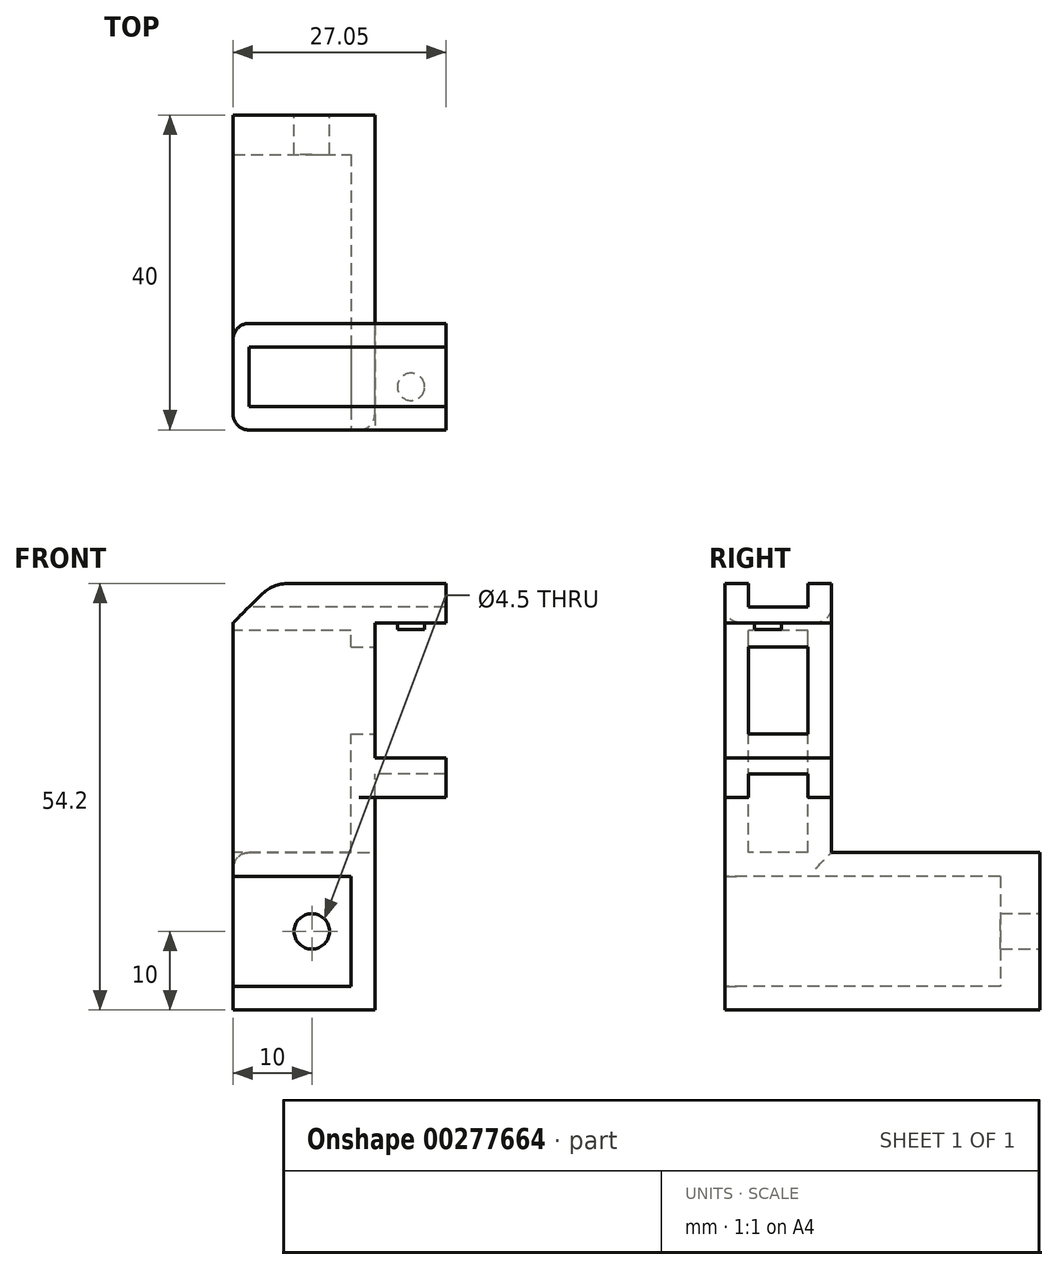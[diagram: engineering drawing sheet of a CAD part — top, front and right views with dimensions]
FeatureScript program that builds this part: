
annotation { "Feature Type Name" : "Feature", "Feature Type Description" : "" }
export const myFeature = defineFeature(function(context is Context, id is Id, definition is map)
    precondition{}
    {
        {
            var Q0;
            Q0=qCreatedBy(makeId("Front.planeOp"),FACE);
            var sketch = newSketch(context, id + "F0", { "sketchPlane" : qUnion([Q0])});
            skLineSegment(sketch, "E0.bottom", {"start": v(0, 0) * mm, "end": v(18, 0) * mm});
            skLineSegment(sketch, "E0.top", {"start": v(0, -21.2) * mm, "end": v(18, -21.2) * mm});
            skLineSegment(sketch, "E0.left", {"start": v(0, 0) * mm, "end": v(0, -21.2) * mm});
            skLineSegment(sketch, "E0.right", {"start": v(18, 0) * mm, "end": v(18, -21.2) * mm});
            skSolve(sketch);
        }
        {
            var Q0;
            Q0 = qSketchRegion(id + "F0", true);
            extrude(context, id + "F1", {"entities" : qUnion([Q0]), "depth" : 40 * mm});
        }
        {
            var Q0;
            Q0=makeQuery(id+"F1.opExtrude","SWEPT_FACE",FACE,{"disambiguationData":[OSD([sQuery(id+"F0.wireOp",EDGE,"E0.right")])]});
            var sketch = newSketch(context, id + "F2", { "sketchPlane" : qUnion([Q0])});
            skLineSegment(sketch, "E1", {"start": v(-40, 0) * mm, "end": v(-26.47, 0) * mm});
            skLineSegment(sketch, "E2", {"start": v(-40, -21.2) * mm, "end": v(-26.47, -21.2) * mm});
            skLineSegment(sketch, "E3", {"start": v(-40, -21.2) * mm, "end": v(-40, -19.15) * mm});
            skLineSegment(sketch, "E4", {"start": v(-26.47, 0) * mm, "end": v(-26.47, -2.05) * mm});
            skLineSegment(sketch, "E5", {"start": v(-26.47, -2.05) * mm, "end": v(-40, -2.05) * mm});
            skLineSegment(sketch, "E6", {"start": v(-40, -2.05) * mm, "end": v(-40, 0) * mm});
            skLineSegment(sketch, "E7", {"start": v(-26.47, -21.2) * mm, "end": v(-26.47, -19.15) * mm});
            skLineSegment(sketch, "E8", {"start": v(-26.47, -19.15) * mm, "end": v(-40, -19.15) * mm});
            skSolve(sketch);
        }
        {
            var Q0;
            Q0 = qSketchRegion(id + "F2", true);
            extrude(context, id + "F3", {"entities" : qUnion([Q0]), "operationType" : NewBodyOperationType.ADD, "depth" : (9.15 - 0.1) * mm});
        }
        {
            var Q0;
            Q0=makeQuery(id+"F3.opExtrude","SWEPT_FACE",FACE,{"disambiguationData":[OSD([sQuery(id+"F2.wireOp",EDGE,"E5")])]});
            var sketch = newSketch(context, id + "F4", { "sketchPlane" : qUnion([Q0])});
            skCircle(sketch, "E9", {"center": v(22.6, 34.53) * mm, "radius": 1.73 * mm});
            skSolve(sketch);
        }
        {
            var Q0;
            Q0 = qSketchRegion(id + "F4", true);
            extrude(context, id + "F5", {"entities" : qUnion([Q0]), "operationType" : NewBodyOperationType.ADD, "depth" : (1 - 0.2) * mm});
        }
        {
            var Q0;
            Q0=makeQuery(id+"F3.opExtrude","SWEPT_FACE",FACE,{"disambiguationData":[OSD([sQuery(id+"F2.wireOp",EDGE,"E5")])]});
            var Q1;
            Q1=makeQuery(id+"F3.opExtrude","SWEPT_FACE",FACE,{"disambiguationData":[OSD([sQuery(id+"F2.wireOp",EDGE,"E8")])]});
            cPlane(context, id + "F6", {"entities" : qUnion([Q0, Q1]), "cplaneType" : CPlaneType.MID_PLANE, "offset" : 25 * mm, "width" : 150 * mm, "height" : 150 * mm});
        }
        {
            var Q0;
            Q0=makeQuery(id+"F3.boolean.opBoolean","MERGE",FACE,{"derivedFrom":[makeQuery(id+"F1.opExtrude","SWEPT_FACE",FACE,{"disambiguationData":[OSD([sQuery(id+"F0.wireOp",EDGE,"E0.top")])]}),makeQuery(id+"F3.opExtrude","SWEPT_FACE",FACE,{"disambiguationData":[OSD([sQuery(id+"F2.wireOp",EDGE,"E2")])]})]});
            var sketch = newSketch(context, id + "F7", { "sketchPlane" : qUnion([Q0])});
            skLineSegment(sketch, "E10.bottom", {"start": v(0, 40) * mm, "end": v(18, 40) * mm});
            skLineSegment(sketch, "E10.top", {"start": v(0, 26.47) * mm, "end": v(18, 26.47) * mm});
            skLineSegment(sketch, "E10.left", {"start": v(0, 40) * mm, "end": v(0, 26.47) * mm});
            skLineSegment(sketch, "E10.right", {"start": v(18, 40) * mm, "end": v(18, 26.47) * mm});
            skSolve(sketch);
        }
        {
            var Q0;
            Q0=makeQuery(id+"F7.imprint","IMPRINT",FACE,{"disambiguationData":[TD([[makeQuery(id+"F7.imprint","IMPRINT",EDGE,{"derivedFrom":sQuery(id+"F7.wireOp",EDGE,"E10.bottom")}),-1.0]])]});
            extrude(context, id + "F8", {"entities" : qUnion([Q0]), "operationType" : NewBodyOperationType.ADD, "depth" : 30 * mm});
        }
        {
            var Q0;
            Q0=makeQuery(id+"F8.opExtrude","SWEPT_FACE",FACE,{"disambiguationData":[OSD([sQuery(id+"F7.wireOp",EDGE,"E10.top")])]});
            var sketch = newSketch(context, id + "F9", { "sketchPlane" : qUnion([Q0])});
            skLineSegment(sketch, "E11.bottom", {"start": v(0, -51.2) * mm, "end": v(-18, -51.2) * mm});
            skLineSegment(sketch, "E11.top", {"start": v(0, -31.2) * mm, "end": v(-18, -31.2) * mm});
            skLineSegment(sketch, "E11.left", {"start": v(0, -51.2) * mm, "end": v(0, -31.2) * mm});
            skLineSegment(sketch, "E11.right", {"start": v(-18, -51.2) * mm, "end": v(-18, -31.2) * mm});
            skSolve(sketch);
        }
        {
            var Q0;
            Q0 = qSketchRegion(id + "F9", true);
            var Q1;
            Q1=qCreatedBy(makeId("Origin.pointOp"),VERTEX);
            extrude(context, id + "F10", {"entities" : qUnion([Q0]), "operationType" : NewBodyOperationType.ADD, "endBound" : BoundingType.UP_TO_VERTEX, "endBoundEntityVertex" : qUnion([Q1]), "depth" : 25 * mm});
        }
        {
            var Q0;
            {var subQ1=sQuery(id+"F0.wireOp",EDGE,"E0.left");var subQ2=sQuery(id+"F0.wireOp",EDGE,"E0.top");var subQ3=makeQuery(id+"F1.opExtrude","SWEPT_FACE",FACE,{"disambiguationData":[OSD([subQ2])]});var subQ4=makeQuery(id+"F3.opExtrude","SWEPT_FACE",FACE,{"disambiguationData":[OSD([sQuery(id+"F2.wireOp",EDGE,"E2")])]});Q0=makeQuery(id+"F8.boolean.opBoolean","SPLIT",FACE,{"disambiguationData":[TD([makeQuery(id+"F1.opExtrude","SWEPT_FACE",FACE,{"disambiguationData":[OSD([subQ1])]})])],"derivedFrom":makeQuery(id+"F3.boolean.opBoolean","MERGE",FACE,{"derivedFrom":[subQ3,subQ4]})});}
            var sketch = newSketch(context, id + "F11", { "sketchPlane" : qUnion([Q0])});
            skLineSegment(sketch, "E12.0.0", {"start": v(18, 26.47) * mm, "end": v(0, 26.47) * mm});
            skLineSegment(sketch, "E12.0.1", {"start": v(0, 26.47) * mm, "end": v(0, 0) * mm});
            skLineSegment(sketch, "E12.0.2", {"start": v(0, 0) * mm, "end": v(18, 0) * mm});
            skLineSegment(sketch, "E12.0.3", {"start": v(18, 0) * mm, "end": v(18, 26.47) * mm});
            skSolve(sketch);
        }
        {
            var Q0;
            Q0 = qSketchRegion(id + "F11", true);
            extrude(context, id + "F12", {"entities" : qUnion([Q0]), "operationType" : NewBodyOperationType.REMOVE, "endBound" : BoundingType.UP_TO_NEXT, "oppositeDirection" : true, "depth" : 25 * mm});
        }
        {
            var Q0;
            Q0=makeQuery(id+"F8.boolean.opBoolean","MERGE",FACE,{"derivedFrom":[makeQuery(id+"F3.boolean.opBoolean","MERGE",FACE,{"derivedFrom":[makeQuery(id+"F1.opExtrude","CAP_FACE",FACE,{"disambiguationData":[OSD([sQuery(id+"F0.wireOp",EDGE,"E0.bottom"),sQuery(id+"F0.wireOp",EDGE,"E0.top"),sQuery(id+"F0.wireOp",EDGE,"E0.left"),sQuery(id+"F0.wireOp",EDGE,"E0.right")])],"isStart":false}),makeQuery(id+"F3.opExtrude","SWEPT_FACE",FACE,{"disambiguationData":[OSD([sQuery(id+"F2.wireOp",EDGE,"E3")])]}),makeQuery(id+"F3.opExtrude","SWEPT_FACE",FACE,{"disambiguationData":[OSD([sQuery(id+"F2.wireOp",EDGE,"E6")])]})]}),makeQuery(id+"F8.opExtrude","SWEPT_FACE",FACE,{"disambiguationData":[OSD([sQuery(id+"F7.wireOp",EDGE,"E10.bottom")])]})]});
            var sketch = newSketch(context, id + "F13", { "sketchPlane" : qUnion([Q0])});
            skLineSegment(sketch, "E13.bottom", {"start": v(0, -34.2) * mm, "end": v(15, -34.2) * mm});
            skLineSegment(sketch, "E13.top", {"start": v(0, -48.2) * mm, "end": v(15, -48.2) * mm});
            skLineSegment(sketch, "E13.left", {"start": v(0, -34.2) * mm, "end": v(0, -48.2) * mm});
            skLineSegment(sketch, "E13.right", {"start": v(15, -34.2) * mm, "end": v(15, -48.2) * mm});
            skPoint(sketch, "E14.0", {"position": v(0, -31.2) * mm});
            skLineSegment(sketch, "E15", {"start": v(0, -34.2) * mm, "end": v(0, -31.2) * mm, "construction": true});
            skLineSegment(sketch, "E16", {"start": v(0, -48.2) * mm, "end": v(0, -51.2) * mm, "construction": true});
            skSolve(sketch);
        }
        {
            var Q0;
            Q0 = qSketchRegion(id + "F13", true);
            extrude(context, id + "F14", {"entities" : qUnion([Q0]), "operationType" : NewBodyOperationType.REMOVE, "oppositeDirection" : true, "depth" : (40 - 5) * mm});
        }
        {
            var Q0;
            Q0=makeQuery(id+"F10.opExtrude","CAP_FACE",FACE,{"disambiguationData":[OSD([sQuery(id+"F9.wireOp",EDGE,"E11.bottom"),sQuery(id+"F9.wireOp",EDGE,"E11.top"),sQuery(id+"F9.wireOp",EDGE,"E11.left"),sQuery(id+"F9.wireOp",EDGE,"E11.right")])],"isStart":false});
            var sketch = newSketch(context, id + "F15", { "sketchPlane" : qUnion([Q0])});
            skLineSegment(sketch, "E17", {"start": v(0, -41.2) * mm, "end": v(-10, -41.2) * mm, "construction": true});
            skPoint(sketch, "E17.endSnap0", {"position": v(0, -41.2) * mm});
            skSolve(sketch);
        }
        {
            var Q0;
            Q0=sQuery(id+"F15.wireOp",VERTEX,"E17.end");
            var Q1;
            Q1=makeQuery(id+"F1.opExtrude","SWEPT_BODY",BODY,{"disambiguationData":[OSD([sQuery(id+"F0.wireOp",EDGE,"E0.bottom"),sQuery(id+"F0.wireOp",EDGE,"E0.top"),sQuery(id+"F0.wireOp",EDGE,"E0.left"),sQuery(id+"F0.wireOp",EDGE,"E0.right")])]});
            hole(context, id + "F16", {"style" : HoleStyle.SIMPLE, "endStyle" : HoleEndStyle.THROUGH, "holeDiameter" : 4.5 * mm, "tappedDepth" : 12 * mm, "tapClearance" : 3, "locations" : qUnion([Q0]), "scope" : qUnion([Q1])});
        }
        {
            var Q0;
            Q0=makeQuery(id+"F10.boolean.opBoolean","MERGE",FACE,{"derivedFrom":[makeQuery(id+"F8.boolean.opBoolean","MERGE",FACE,{"derivedFrom":[makeQuery(id+"F1.opExtrude","SWEPT_FACE",FACE,{"disambiguationData":[OSD([sQuery(id+"F0.wireOp",EDGE,"E0.left")])]}),makeQuery(id+"F8.opExtrude","SWEPT_FACE",FACE,{"disambiguationData":[OSD([sQuery(id+"F7.wireOp",EDGE,"E10.left")])]})]}),makeQuery(id+"F10.opExtrude","SWEPT_FACE",FACE,{"disambiguationData":[OSD([sQuery(id+"F9.wireOp",EDGE,"E11.left")])]})]});
            var sketch = newSketch(context, id + "F17", { "sketchPlane" : qUnion([Q0])});
            skLineSegment(sketch, "E18", {"start": v(33.24, 0) * mm, "end": v(33.24, -34.2) * mm, "construction": true});
            skLineSegment(sketch, "E19", {"start": v(26.47, -15.6) * mm, "end": v(40, -15.6) * mm, "construction": true});
            skLineSegment(sketch, "E20", {"start": v(26.47, -31.2) * mm, "end": v(40, -31.2) * mm, "construction": true});
            skLineSegment(sketch, "E21.bottom", {"start": v(29.48, -31.2) * mm, "end": v(37, -31.2) * mm});
            skLineSegment(sketch, "E21.top", {"start": v(29.47, -3) * mm, "end": v(37, -3) * mm});
            skLineSegment(sketch, "E21.left", {"start": v(29.48, -31.2) * mm, "end": v(29.47, -3) * mm});
            skLineSegment(sketch, "E21.right", {"start": v(37, -31.2) * mm, "end": v(37, -3) * mm});
            skSolve(sketch);
        }
        {
            var Q0;
            Q0 = qSketchRegion(id + "F17", true);
            extrude(context, id + "F18", {"entities" : qUnion([Q0]), "operationType" : NewBodyOperationType.REMOVE, "oppositeDirection" : true, "depth" : (18 - 3) * mm});
        }
        {
            var Q0;
            Q0=makeQuery(id+"F1.opExtrude","SWEPT_FACE",FACE,{"disambiguationData":[OSD([sQuery(id+"F0.wireOp",EDGE,"E0.right")])]});
            var sketch = newSketch(context, id + "F19", { "sketchPlane" : qUnion([Q0])});
            skLineSegment(sketch, "E22.bottom", {"start": v(-37, -5.05) * mm, "end": v(-29.47, -5.05) * mm});
            skLineSegment(sketch, "E22.top", {"start": v(-37, -16.15) * mm, "end": v(-29.47, -16.15) * mm});
            skLineSegment(sketch, "E22.left", {"start": v(-37, -5.05) * mm, "end": v(-37, -16.15) * mm});
            skLineSegment(sketch, "E22.right", {"start": v(-29.47, -5.05) * mm, "end": v(-29.47, -16.15) * mm});
            skSolve(sketch);
        }
        {
            var Q0;
            Q0 = qSketchRegion(id + "F19", true);
            extrude(context, id + "F20", {"entities" : qUnion([Q0]), "operationType" : NewBodyOperationType.REMOVE, "endBound" : BoundingType.THROUGH_ALL, "oppositeDirection" : true, "depth" : 25 * mm});
        }
        {
            var Q0;
            Q0=makeQuery(id+"F3.boolean.opBoolean","MERGE",FACE,{"derivedFrom":[makeQuery(id+"F1.opExtrude","SWEPT_FACE",FACE,{"disambiguationData":[OSD([sQuery(id+"F0.wireOp",EDGE,"E0.bottom")])]}),makeQuery(id+"F3.opExtrude","SWEPT_FACE",FACE,{"disambiguationData":[OSD([sQuery(id+"F2.wireOp",EDGE,"E1")])]})]});
            var sketch = newSketch(context, id + "F21", { "sketchPlane" : qUnion([Q0])});
            skLineSegment(sketch, "E23.bottom", {"start": v(27.05, -40) * mm, "end": v(0, -40) * mm});
            skLineSegment(sketch, "E23.top", {"start": v(27.05, -37) * mm, "end": v(0, -37) * mm});
            skLineSegment(sketch, "E23.left", {"start": v(27.05, -40) * mm, "end": v(27.05, -37) * mm});
            skLineSegment(sketch, "E23.right", {"start": v(0, -40) * mm, "end": v(0, -37) * mm});
            skLineSegment(sketch, "E24.bottom", {"start": v(27.05, -26.47) * mm, "end": v(0, -26.47) * mm});
            skLineSegment(sketch, "E24.top", {"start": v(27.05, -29.47) * mm, "end": v(0, -29.47) * mm});
            skLineSegment(sketch, "E24.left", {"start": v(27.05, -26.47) * mm, "end": v(27.05, -29.47) * mm});
            skLineSegment(sketch, "E24.right", {"start": v(0, -26.47) * mm, "end": v(0, -29.47) * mm});
            skSolve(sketch);
        }
        {
            var Q0;
            Q0 = qSketchRegion(id + "F21", true);
            extrude(context, id + "F22", {"entities" : qUnion([Q0]), "operationType" : NewBodyOperationType.ADD, "depth" : 3 * mm});
        }
        {
            var Q0;
            {var subQ0=sQuery(id+"F2.wireOp",EDGE,"E2");var subQ1=makeQuery(id+"F3.opExtrude","SWEPT_FACE",FACE,{"disambiguationData":[OSD([subQ0])]});var subQ2=sQuery(id+"F2.wireOp",EDGE,"E3");var subQ5=sQuery(id+"F0.wireOp",EDGE,"E0.top");var subQ6=makeQuery(id+"F1.opExtrude","SWEPT_FACE",FACE,{"disambiguationData":[OSD([subQ5])]});Q0=makeQuery(id+"F8.boolean.opBoolean","SPLIT",FACE,{"disambiguationData":[TD([makeQuery(id+"F3.opExtrude","SWEPT_FACE",FACE,{"disambiguationData":[OSD([subQ2])]})])],"derivedFrom":makeQuery(id+"F3.boolean.opBoolean","MERGE",FACE,{"derivedFrom":[subQ6,subQ1]})});}
            var sketch = newSketch(context, id + "F23", { "sketchPlane" : qUnion([Q0])});
            skLineSegment(sketch, "E25.bottom", {"start": v(27.05, 40) * mm, "end": v(18, 40) * mm});
            skLineSegment(sketch, "E25.top", {"start": v(27.05, 37) * mm, "end": v(18, 37) * mm});
            skLineSegment(sketch, "E25.left", {"start": v(27.05, 40) * mm, "end": v(27.05, 37) * mm});
            skLineSegment(sketch, "E25.right", {"start": v(18, 40) * mm, "end": v(18, 37) * mm});
            skLineSegment(sketch, "E26.bottom", {"start": v(27.05, 26.47) * mm, "end": v(18, 26.47) * mm});
            skLineSegment(sketch, "E26.top", {"start": v(27.05, 29.47) * mm, "end": v(18, 29.47) * mm});
            skLineSegment(sketch, "E26.left", {"start": v(27.05, 26.47) * mm, "end": v(27.05, 29.47) * mm});
            skLineSegment(sketch, "E26.right", {"start": v(18, 26.47) * mm, "end": v(18, 29.47) * mm});
            skSolve(sketch);
        }
        {
            var Q0;
            Q0 = qSketchRegion(id + "F23", true);
            extrude(context, id + "F24", {"entities" : qUnion([Q0]), "operationType" : NewBodyOperationType.ADD, "depth" : 3 * mm});
        }
        {
            var Q0;
            Q0=makeQuery(id+"F22.opExtrude","CAP_EDGE",EDGE,{"disambiguationData":[OSD([sQuery(id+"F21.wireOp",EDGE,"E24.right")])],"isStart":false});
            chamfer(context, id + "F25", {"entities" : qUnion([Q0]), "width" : 5 * mm, "tangentPropagation" : true});
        }
        {
            var Q0;
            {var subQ0=sQuery(id+"F0.wireOp",EDGE,"E0.left");var subQ1=sQuery(id+"F7.wireOp",EDGE,"E10.bottom");var subQ2=sQuery(id+"F7.wireOp",EDGE,"E10.left");Q0=makeQuery(id+"F14.boolean.opBoolean","SPLIT",EDGE,{"disambiguationData":[TD([makeQuery(id+"F10.opExtrude","SWEPT_FACE",FACE,{"disambiguationData":[OSD([sQuery(id+"F9.wireOp",EDGE,"E11.bottom")])]})])],"derivedFrom":makeQuery(id+"F8.boolean.opBoolean","MERGE",EDGE,{"derivedFrom":[makeQuery(id+"F1.opExtrude","CAP_EDGE",EDGE,{"disambiguationData":[OSD([subQ0])],"isStart":false}),makeQuery(id+"F8.opExtrude","SWEPT_EDGE",EDGE,{"disambiguationData":[OSD([subQ1,subQ2])]})]})});}
            var Q1;
            {var subQ0=sQuery(id+"F0.wireOp",EDGE,"E0.left");var subQ1=sQuery(id+"F0.wireOp",EDGE,"E0.bottom");var subQ2=sQuery(id+"F7.wireOp",EDGE,"E10.bottom");var subQ3=sQuery(id+"F7.wireOp",EDGE,"E10.left");Q1=makeQuery(id+"F14.boolean.opBoolean","SPLIT",EDGE,{"disambiguationData":[TD([makeQuery(id+"F1.opExtrude","SWEPT_FACE",FACE,{"disambiguationData":[OSD([subQ1])]})])],"derivedFrom":makeQuery(id+"F8.boolean.opBoolean","MERGE",EDGE,{"derivedFrom":[makeQuery(id+"F1.opExtrude","CAP_EDGE",EDGE,{"disambiguationData":[OSD([subQ0])],"isStart":false}),makeQuery(id+"F8.opExtrude","SWEPT_EDGE",EDGE,{"disambiguationData":[OSD([subQ2,subQ3])]})]})});}
            var Q2;
            Q2=makeQuery(id+"F1.opExtrude","SWEPT_EDGE",EDGE,{"disambiguationData":[OSD([sQuery(id+"F0.wireOp",EDGE,"E0.bottom"),sQuery(id+"F0.wireOp",EDGE,"E0.left")])]});
            var Q3;
            Q3=makeQuery(id+"F10.opExtrude","SWEPT_EDGE",EDGE,{"disambiguationData":[OSD([sQuery(id+"F0.wireOp",EDGE,"E0.top"),sQuery(id+"F0.wireOp",EDGE,"E0.left"),sQuery(id+"F7.wireOp",EDGE,"E10.top"),sQuery(id+"F7.wireOp",EDGE,"E10.left"),sQuery(id+"F9.wireOp",EDGE,"E11.top"),sQuery(id+"F9.wireOp",EDGE,"E11.left")])]});
            var Q4;
            Q4=makeQuery(id+"F8.opExtrude","SWEPT_EDGE",EDGE,{"disambiguationData":[OSD([sQuery(id+"F0.wireOp",EDGE,"E0.top"),sQuery(id+"F2.wireOp",EDGE,"E2"),sQuery(id+"F2.wireOp",EDGE,"E3"),sQuery(id+"F7.wireOp",EDGE,"E10.bottom"),sQuery(id+"F7.wireOp",EDGE,"E10.right")])]});
            var Q5;
            {var subQ0=sQuery(id+"F7.wireOp",EDGE,"E10.left");var subQ1=sQuery(id+"F7.wireOp",EDGE,"E10.top");var subQ2=sQuery(id+"F0.wireOp",EDGE,"E0.left");var subQ3=sQuery(id+"F0.wireOp",EDGE,"E0.top");Q5=makeQuery(id+"F22.boolean.opBoolean","MERGE",EDGE,{"derivedFrom":[makeQuery(id+"F12.boolean.opBoolean","MERGE",EDGE,{"derivedFrom":[makeQuery(id+"F8.opExtrude","SWEPT_EDGE",EDGE,{"disambiguationData":[OSD([subQ3,subQ2,subQ1,subQ0])]})],"fromTools":[makeQuery(id+"F12.opExtrude","SWEPT_EDGE",EDGE,{"disambiguationData":[OSD([subQ3,subQ2,subQ1,subQ0,sQuery(id+"F11.wireOp",EDGE,"E12.0.0"),sQuery(id+"F11.wireOp",EDGE,"E12.0.1")])]})]}),makeQuery(id+"F22.opExtrude","SWEPT_EDGE",EDGE,{"disambiguationData":[OSD([sQuery(id+"F21.wireOp",EDGE,"E24.bottom"),sQuery(id+"F21.wireOp",EDGE,"E24.right")])]})]});}
            fillet(context, id + "F26", {"entities" : qUnion([Q0, Q1, Q2, Q3, Q4, Q5]), "radius" : 2 * mm, "tangentPropagation" : true, "allowEdgeOverflow" : false});
        }
        {
            var Q0;
            Q0=makeQuery(id+"F25.opChamfer","BLEND_EDGE",EDGE,{"blendedFrom":[makeQuery(id+"F22.opExtrude","CAP_EDGE",EDGE,{"disambiguationData":[OSD([sQuery(id+"F21.wireOp",EDGE,"E24.right")])],"isStart":false}),makeQuery(id+"F22.opExtrude","CAP_FACE",FACE,{"disambiguationData":[OSD([sQuery(id+"F21.wireOp",EDGE,"E23.bottom"),sQuery(id+"F21.wireOp",EDGE,"E23.top"),sQuery(id+"F21.wireOp",EDGE,"E23.left"),sQuery(id+"F21.wireOp",EDGE,"E23.right")])],"isStart":false})],"blendedInto":[makeQuery(id+"F22.opExtrude","CAP_FACE",FACE,{"disambiguationData":[OSD([sQuery(id+"F21.wireOp",EDGE,"E23.bottom"),sQuery(id+"F21.wireOp",EDGE,"E23.top"),sQuery(id+"F21.wireOp",EDGE,"E23.left"),sQuery(id+"F21.wireOp",EDGE,"E23.right")])],"isStart":false})]});
            var Q1;
            {var subQ0=sQuery(id+"F21.wireOp",EDGE,"E24.right");Q1=makeQuery(id+"F25.opChamfer","BLEND_EDGE",EDGE,{"blendedFrom":[makeQuery(id+"F22.opExtrude","CAP_EDGE",EDGE,{"disambiguationData":[OSD([subQ0])],"isStart":false}),makeQuery(id+"F22.opExtrude","CAP_FACE",FACE,{"disambiguationData":[OSD([sQuery(id+"F21.wireOp",EDGE,"E24.bottom"),sQuery(id+"F21.wireOp",EDGE,"E24.top"),sQuery(id+"F21.wireOp",EDGE,"E24.left"),subQ0])],"isStart":false})],"blendedInto":[makeQuery(id+"F22.opExtrude","CAP_FACE",FACE,{"disambiguationData":[OSD([sQuery(id+"F21.wireOp",EDGE,"E24.bottom"),sQuery(id+"F21.wireOp",EDGE,"E24.top"),sQuery(id+"F21.wireOp",EDGE,"E24.left"),subQ0])],"isStart":false})]});}
            fillet(context, id + "F27", {"entities" : qUnion([Q0, Q1]), "radius" : 5 * mm, "tangentPropagation" : true, "allowEdgeOverflow" : false});
        }
    });
